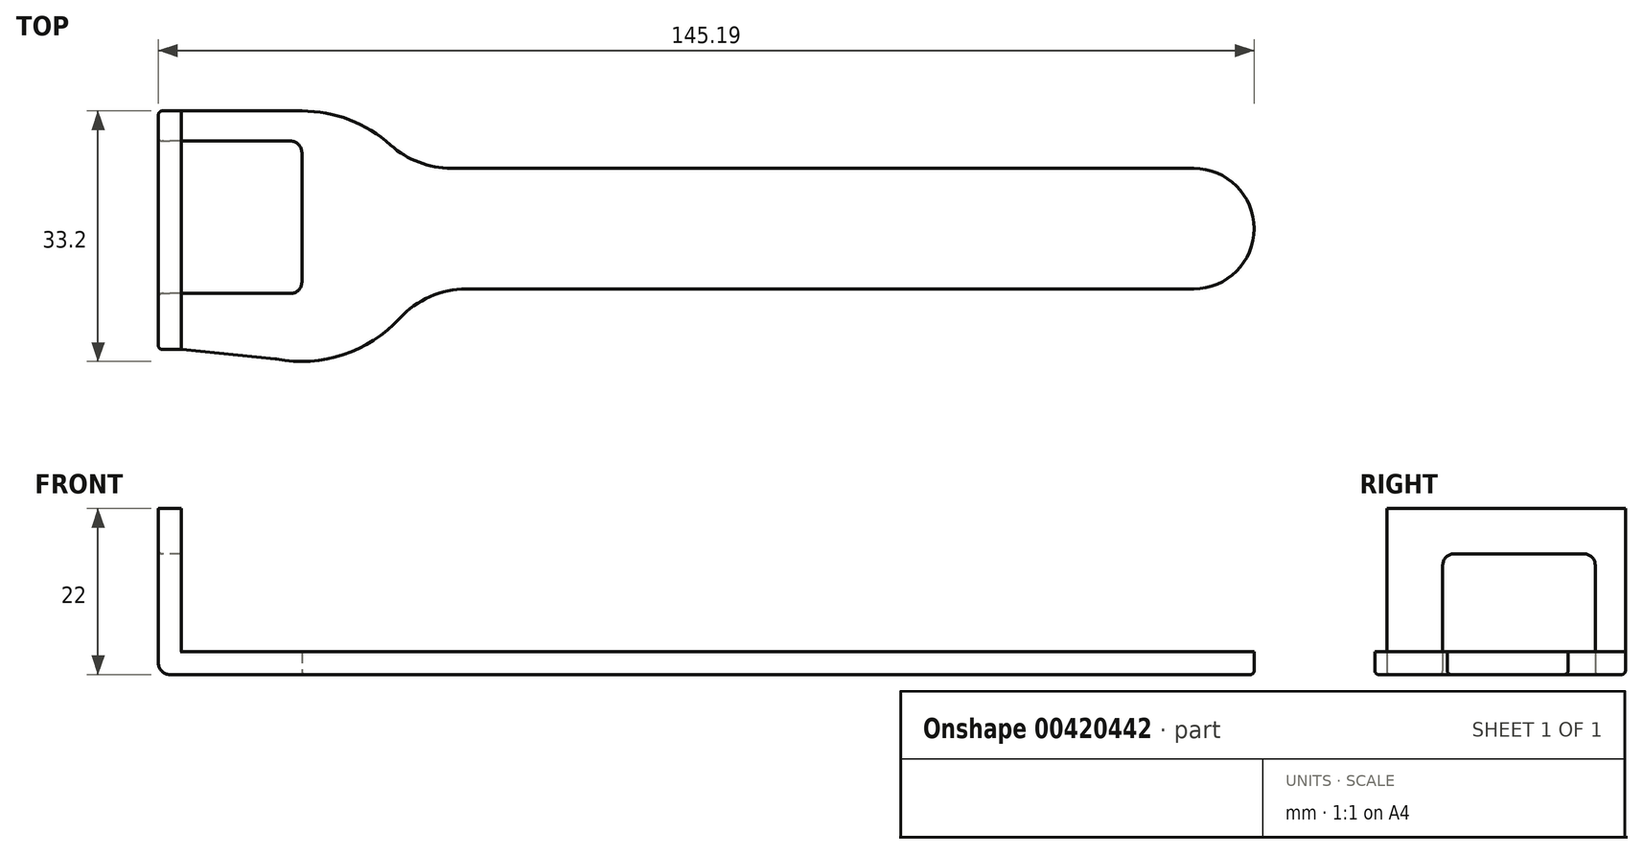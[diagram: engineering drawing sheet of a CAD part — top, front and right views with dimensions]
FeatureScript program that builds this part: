
annotation { "Feature Type Name" : "Feature", "Feature Type Description" : "" }
export const myFeature = defineFeature(function(context is Context, id is Id, definition is map)
    precondition{}
    {
        {
            var Q0;
            Q0=qCreatedBy(makeId("Top.planeOp"),FACE);
            var sketch = newSketch(context, id + "F0", { "sketchPlane" : qUnion([Q0])});
            skArc(sketch, "E0", {"start": v(-73.97, -17.26) * mm, "mid": v(-62.86, -15.84) * mm, "end": v(-54.85, -8) * mm});
            skLineSegment(sketch, "E1", {"start": v(59.4, -20.35) * mm, "end": v(59.4, 16.2) * mm, "construction": true});
            skLineSegment(sketch, "E2", {"start": v(-86.52, 35.8) * mm, "end": v(-86.52, -38.11) * mm, "construction": true});
            skLineSegment(sketch, "E3.top", {"start": v(-70.52, -17.6) * mm, "end": v(-50.32, -17.6) * mm, "construction": true});
            skLineSegment(sketch, "E3.right", {"start": v(-50.32, 17.6) * mm, "end": v(-50.32, -17.6) * mm, "construction": true});
            skLineSegment(sketch, "E4.top", {"start": v(-70.52, 11.6) * mm, "end": v(-86.52, 11.6) * mm});
            skLineSegment(sketch, "E5.top", {"start": v(-70.52, -8.6) * mm, "end": v(-86.52, -8.6) * mm});
            skLineSegment(sketch, "E6", {"start": v(-63.17, 15.6) * mm, "end": v(-86.52, 15.6) * mm});
            skLineSegment(sketch, "E7", {"start": v(-70.52, -17.6) * mm, "end": v(-86.52, -16.02) * mm});
            skLineSegment(sketch, "E8", {"start": v(-70.52, -8.6) * mm, "end": v(-70.52, 11.6) * mm});
            skLineSegment(sketch, "E9", {"start": v(-98.89, 0) * mm, "end": v(66.7, 0) * mm, "construction": true});
            skArc(sketch, "E10", {"start": v(47.67, -8) * mm, "mid": v(55.67, 0) * mm, "end": v(47.67, 8) * mm});
            skLineSegment(sketch, "E11", {"start": v(47.67, 8) * mm, "end": v(-50.32, 8) * mm});
            skLineSegment(sketch, "E12", {"start": v(47.67, -8) * mm, "end": v(-54.85, -8) * mm});
            skPoint(sketch, "E13.end.orphan", {"position": v(-61.1, 8) * mm});
            skPoint(sketch, "E14.orphan", {"position": v(-62.74, 8) * mm});
            skArc(sketch, "E15.trimOffspring", {"start": v(-56.04, 8) * mm, "mid": v(-62.35, 13.58) * mm, "end": v(-70.52, 15.6) * mm});
            skLineSegment(sketch, "E16", {"start": v(-50.32, 8) * mm, "end": v(-56.04, 8) * mm});
            skLineSegment(sketch, "E17.right", {"start": v(-86.52, 15.6) * mm, "end": v(-86.52, 11.6) * mm});
            skLineSegment(sketch, "E18.trimOffspring", {"start": v(-86.52, 15.6) * mm, "end": v(-46.92, 15.6) * mm, "construction": true});
            skLineSegment(sketch, "E19", {"start": v(-86.52, -8.6) * mm, "end": v(-86.52, -16.02) * mm});
            skSolve(sketch);
        }
        {
            var Q0;
            Q0=qSketchRegion(id+"F0",true);
            extrude(context, id + "F1", {"entities" : qUnion([Q0]), "depth" : 3 * mm});
        }
        {
            var Q0;
            Q0=qCreatedBy(makeId("Top.planeOp"),FACE);
            var sketch = newSketch(context, id + "F2", { "sketchPlane" : qUnion([Q0])});
            skLineSegment(sketch, "E20.bottom", {"start": v(-86.52, 15.6) * mm, "end": v(-89.52, 15.6) * mm});
            skLineSegment(sketch, "E20.top", {"start": v(-86.52, -16.02) * mm, "end": v(-89.52, -16.02) * mm});
            skLineSegment(sketch, "E20.left", {"start": v(-86.52, 15.6) * mm, "end": v(-86.52, -16.02) * mm});
            skLineSegment(sketch, "E20.right", {"start": v(-89.52, 15.6) * mm, "end": v(-89.52, -16.02) * mm});
            skSolve(sketch);
        }
        {
            var Q0;
            Q0 = qSketchRegion(id + "F2", true);
            extrude(context, id + "F3", {"entities" : qUnion([Q0]), "operationType" : NewBodyOperationType.ADD, "depth" : 22 * mm});
        }
        {
            var Q0;
            Q0=qCreatedBy(makeId("Top.planeOp"),FACE);
            var sketch = newSketch(context, id + "F4", { "sketchPlane" : qUnion([Q0])});
            skLineSegment(sketch, "E21.bottom", {"start": v(-86.52, 11.6) * mm, "end": v(-89.52, 11.6) * mm});
            skLineSegment(sketch, "E21.top", {"start": v(-86.52, -8.6) * mm, "end": v(-89.52, -8.6) * mm});
            skLineSegment(sketch, "E21.left", {"start": v(-86.52, 11.6) * mm, "end": v(-86.52, -8.6) * mm});
            skLineSegment(sketch, "E21.right", {"start": v(-89.52, 11.6) * mm, "end": v(-89.52, -8.6) * mm});
            skSolve(sketch);
        }
        {
            var Q0;
            Q0 = qSketchRegion(id + "F4", true);
            extrude(context, id + "F5", {"entities" : qUnion([Q0]), "operationType" : NewBodyOperationType.REMOVE, "depth" : 16 * mm});
        }
        {
            var Q0;
            Q0=makeQuery(id+"F1.opExtrude","SWEPT_EDGE",EDGE,{"disambiguationData":[OSD([sQuery(id+"F0.wireOp",EDGE,"E6"),sQuery(id+"F0.wireOp",EDGE,"JTNi2FiC-B9Hd-yy0C-NibE-VtpdYRL0dKmn")])]});
            var Q1;
            Q1=makeQuery(id+"F1.opExtrude","SWEPT_EDGE",EDGE,{"disambiguationData":[OSD([sQuery(id+"F0.wireOp",EDGE,"E4.top"),sQuery(id+"F0.wireOp",EDGE,"JTNi2FiC-B9Hd-yy0C-NibE-VtpdYRL0dKmn")])]});
            var Q2;
            Q2=makeQuery(id+"F1.opExtrude","SWEPT_EDGE",EDGE,{"disambiguationData":[OSD([sQuery(id+"F0.wireOp",EDGE,"E5.top"),sQuery(id+"F0.wireOp",EDGE,"b8165475-47af-4af3-b4ca-044acb1de50d.trimOffspring")])]});
            var Q3;
            Q3=makeQuery(id+"F1.opExtrude","SWEPT_EDGE",EDGE,{"disambiguationData":[OSD([sQuery(id+"F0.wireOp",EDGE,"b8165475-47af-4af3-b4ca-044acb1de50d.trimOffspring"),sQuery(id+"F0.wireOp",EDGE,"E7")])]});
            var Q4;
            Q4=makeQuery(id+"F1.opExtrude","SWEPT_EDGE",EDGE,{"disambiguationData":[OSD([sQuery(id+"F0.wireOp",EDGE,"E4.top"),sQuery(id+"F0.wireOp",EDGE,"E8")])]});
            var Q5;
            Q5=makeQuery(id+"F1.opExtrude","SWEPT_EDGE",EDGE,{"disambiguationData":[OSD([sQuery(id+"F0.wireOp",EDGE,"E5.top"),sQuery(id+"F0.wireOp",EDGE,"E8")])]});
            var Q6;
            {var subQ0=sQuery(id+"F2.wireOp",EDGE,"E20.right");var subQ2=sQuery(id+"F0.wireOp",EDGE,"E5.top");Q6=makeQuery(id+"F5.boolean.opBoolean","SPLIT",EDGE,{"disambiguationData":[TD([makeQuery(id+"F1.opExtrude","SWEPT_FACE",FACE,{"disambiguationData":[OSD([subQ2])]})])],"derivedFrom":makeQuery(id+"F3.opExtrude","CAP_EDGE",EDGE,{"disambiguationData":[OSD([subQ0])],"isStart":true})});}
            var Q7;
            {var subQ2=sQuery(id+"F0.wireOp",EDGE,"E4.top");var subQ3=sQuery(id+"F2.wireOp",EDGE,"E20.right");Q7=makeQuery(id+"F5.boolean.opBoolean","SPLIT",EDGE,{"disambiguationData":[TD([makeQuery(id+"F1.opExtrude","SWEPT_FACE",FACE,{"disambiguationData":[OSD([subQ2])]})])],"derivedFrom":makeQuery(id+"F3.opExtrude","CAP_EDGE",EDGE,{"disambiguationData":[OSD([subQ3])],"isStart":true})});}
            var Q8;
            Q8=makeQuery(id+"F1.opExtrude","CAP_EDGE",EDGE,{"disambiguationData":[OSD([sQuery(id+"F0.wireOp",EDGE,"E19")])],"isStart":false});
            var Q9;
            Q9=makeQuery(id+"F1.opExtrude","CAP_EDGE",EDGE,{"disambiguationData":[OSD([sQuery(id+"F0.wireOp",EDGE,"E17.right")])],"isStart":false});
            var Q10;
            Q10=makeQuery(id+"F5.boolean.opBoolean","COPY",EDGE,{"derivedFrom":makeQuery(id+"F5.opExtrude","CAP_EDGE",EDGE,{"disambiguationData":[OSD([sQuery(id+"F4.wireOp",EDGE,"E21.bottom")])],"isStart":false})});
            var Q11;
            Q11=makeQuery(id+"F5.boolean.opBoolean","COPY",EDGE,{"derivedFrom":makeQuery(id+"F5.opExtrude","CAP_EDGE",EDGE,{"disambiguationData":[OSD([sQuery(id+"F4.wireOp",EDGE,"E21.top")])],"isStart":false})});
            fillet(context, id + "F6", {"entities" : qUnion([Q0, Q1, Q2, Q3, Q4, Q5, Q6, Q7, Q8, Q9, Q10, Q11]), "radius" : 1.5 * mm, "tangentPropagation" : true, "allowEdgeOverflow" : false});
        }
        {
            var Q0;
            Q0=makeQuery(id+"F1.opExtrude","SWEPT_EDGE",EDGE,{"disambiguationData":[OSD([sQuery(id+"F0.wireOp",EDGE,"E11"),sQuery(id+"F0.wireOp",EDGE,"E15.trimOffspring")])]});
            var Q1;
            Q1=makeQuery(id+"F1.opExtrude","SWEPT_EDGE",EDGE,{"disambiguationData":[OSD([sQuery(id+"F0.wireOp",EDGE,"E0"),sQuery(id+"F0.wireOp",EDGE,"E12")])]});
            fillet(context, id + "F7", {"entities" : qUnion([Q0, Q1]), "radius" : 12 * mm, "tangentPropagation" : true, "allowEdgeOverflow" : false});
        }
        {
            var Q0;
            Q0=makeQuery(id+"F1.opExtrude","CAP_FACE",FACE,{"disambiguationData":[OSD([sQuery(id+"F0.wireOp",EDGE,"E0"),sQuery(id+"F0.wireOp",EDGE,"E4.top"),sQuery(id+"F0.wireOp",EDGE,"E5.top"),sQuery(id+"F0.wireOp",EDGE,"E6"),sQuery(id+"F0.wireOp",EDGE,"JTNi2FiC-B9Hd-yy0C-NibE-VtpdYRL0dKmn"),sQuery(id+"F0.wireOp",EDGE,"b8165475-47af-4af3-b4ca-044acb1de50d.trimOffspring"),sQuery(id+"F0.wireOp",EDGE,"E7"),sQuery(id+"F0.wireOp",EDGE,"E8"),sQuery(id+"F0.wireOp",EDGE,"E10"),sQuery(id+"F0.wireOp",EDGE,"E11"),sQuery(id+"F0.wireOp",EDGE,"E12"),sQuery(id+"F0.wireOp",EDGE,"E15.trimOffspring"),sQuery(id+"F0.wireOp",EDGE,"E16")])],"isStart":true});
            fillet(context, id + "F8", {"entities" : qUnion([Q0]), "radius" : .5 * mm, "tangentPropagation" : true, "allowEdgeOverflow" : false});
        }
    });
